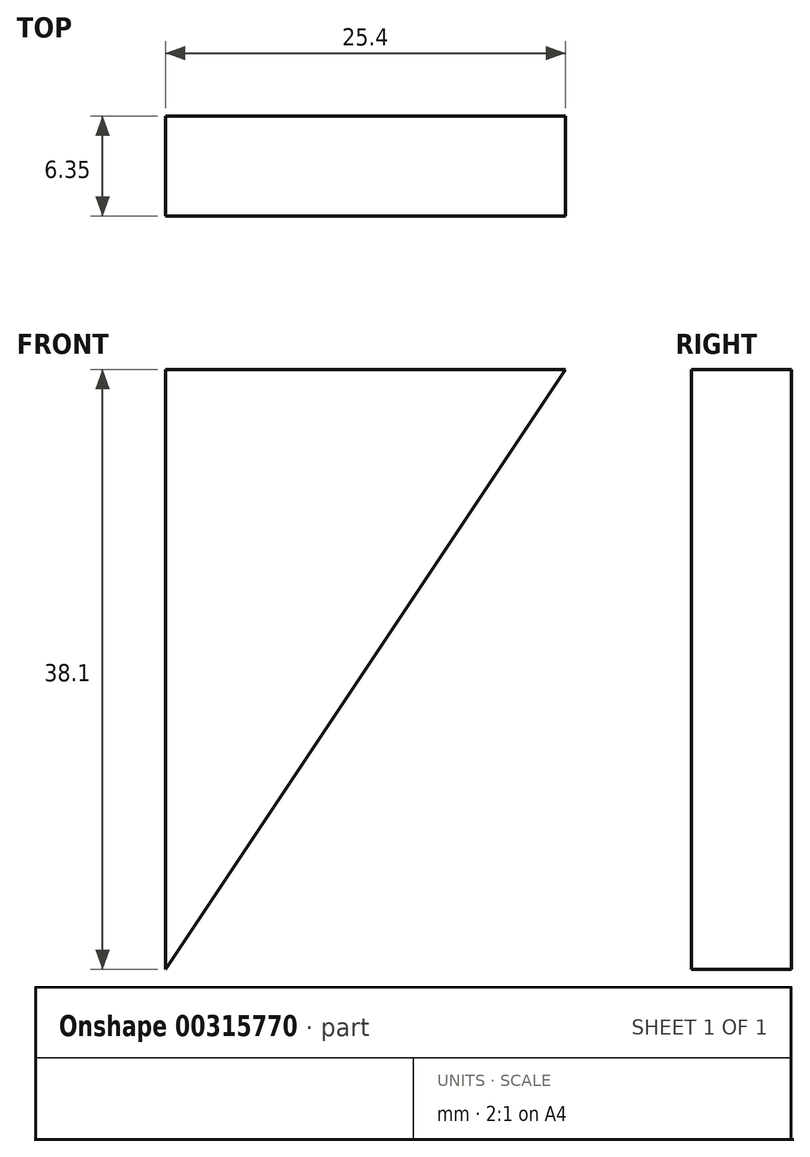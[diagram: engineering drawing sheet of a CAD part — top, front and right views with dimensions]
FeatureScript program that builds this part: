
annotation { "Feature Type Name" : "Feature", "Feature Type Description" : "" }
export const myFeature = defineFeature(function(context is Context, id is Id, definition is map)
    precondition{}
    {
        {
            var Q0;
            Q0=qCreatedBy(makeId("Front.planeOp"),FACE);
            var sketch = newSketch(context, id + "F0", { "sketchPlane" : qUnion([Q0])});
            skLineSegment(sketch, "E0.bottom", {"start": v(0, 0) * mm, "end": v(-25.4, 0) * mm});
            skLineSegment(sketch, "E0.top", {"start": v(0, 38.1) * mm, "end": v(-25.4, 38.1) * mm});
            skLineSegment(sketch, "E0.left", {"start": v(0, 0) * mm, "end": v(0, 38.1) * mm});
            skLineSegment(sketch, "E0.right", {"start": v(-25.4, 0) * mm, "end": v(-25.4, 38.1) * mm});
            skSolve(sketch);
        }
        {
            var Q0;
            Q0=makeQuery(id+"F0.imprint","IMPRINT",FACE,{"disambiguationData":[TD([[makeQuery(id+"F0.imprint","IMPRINT",EDGE,{"derivedFrom":sQuery(id+"F0.wireOp",EDGE,"E0.bottom")}),-1.0]])]});
            var sketch = newSketch(context, id + "F1", { "sketchPlane" : qUnion([Q0])});
            skLineSegment(sketch, "E1", {"start": v(0, 38.1) * mm, "end": v(-25.4, 38.1) * mm});
            skLineSegment(sketch, "E2", {"start": v(-25.4, 38.1) * mm, "end": v(-25.4, 0) * mm});
            skLineSegment(sketch, "E3", {"start": v(-25.4, 0) * mm, "end": v(0, 38.1) * mm});
            skSolve(sketch);
        }
        {
            var Q0;
            Q0=makeQuery(id+"F1.imprint","IMPRINT",FACE,{"disambiguationData":[TD([[makeQuery(id+"F1.imprint","IMPRINT",EDGE,{"derivedFrom":sQuery(id+"F1.wireOp",EDGE,"E1")}),1.0]])]});
            extrude(context, id + "F2", {"entities" : qUnion([Q0]), "depth" : 6.35 * mm});
        }
    });
